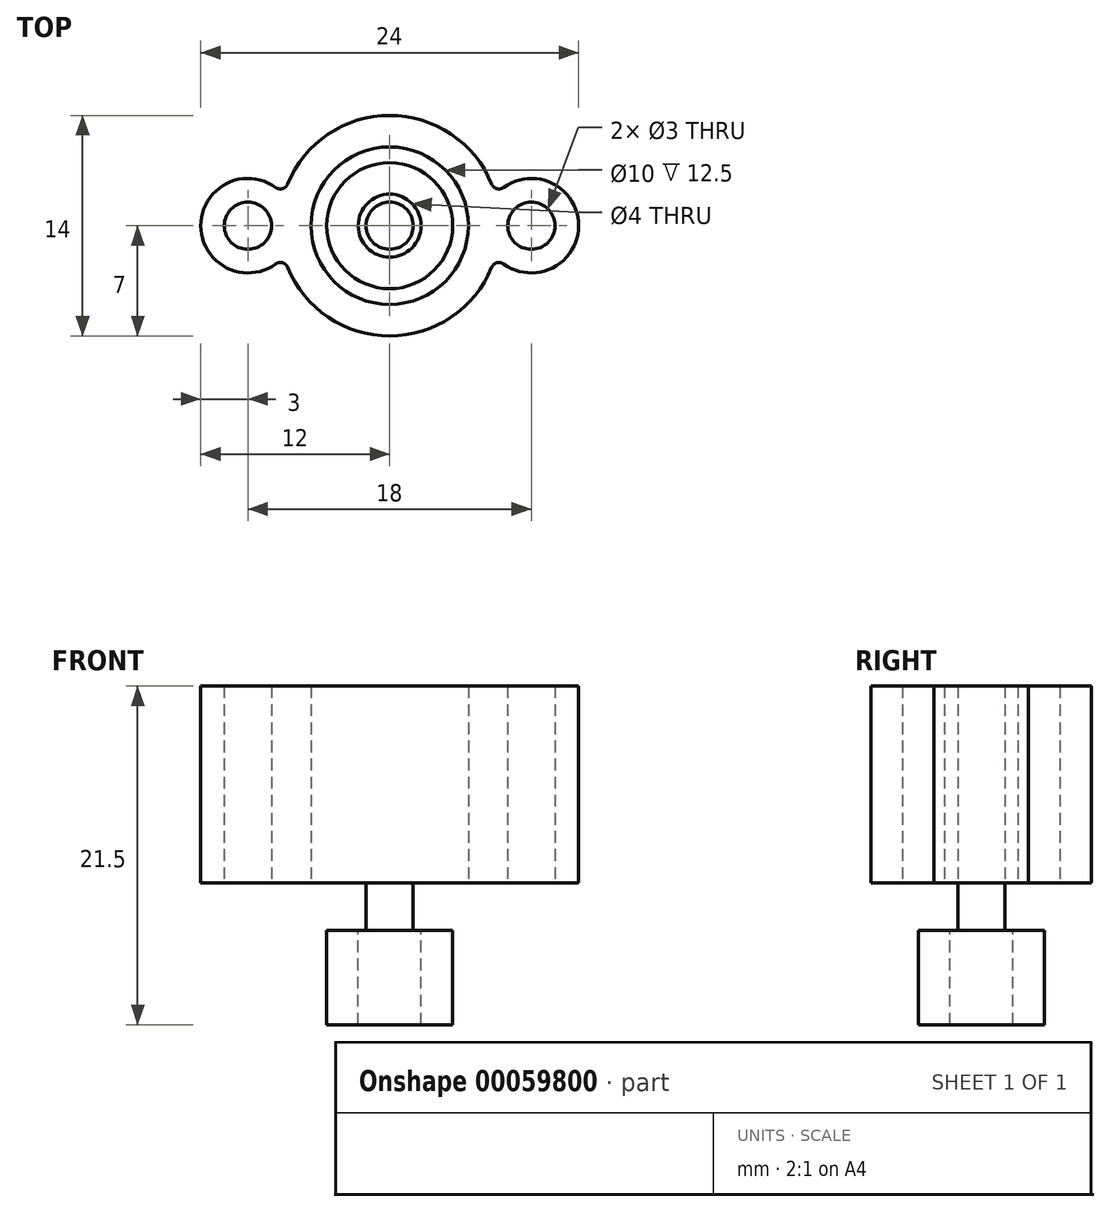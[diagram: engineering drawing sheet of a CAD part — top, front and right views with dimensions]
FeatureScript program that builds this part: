
annotation { "Feature Type Name" : "Feature", "Feature Type Description" : "" }
export const myFeature = defineFeature(function(context is Context, id is Id, definition is map)
    precondition{}
    {
        {
            var Q0;
            Q0=qCreatedBy(makeId("Top.planeOp"),FACE);
            var sketch = newSketch(context, id + "F0", { "sketchPlane" : qUnion([Q0])});
            skCircle(sketch, "E0", {"center": v(9, 0) * mm, "radius": 3 * mm, "construction": true});
            skLineSegment(sketch, "E1", {"start": v(9, 0) * mm, "end": v(0, 0) * mm, "construction": true});
            skLineSegment(sketch, "E2", {"start": v(0, -7) * mm, "end": v(0, 7) * mm, "construction": true});
            skCircle(sketch, "E3", {"center": v(0, 0) * mm, "radius": 7 * mm, "construction": true});
            skArc(sketch, "E4", {"start": v(0, 1.5) * mm, "mid": v(1.5, 0) * mm, "end": v(0, -1.5) * mm});
            skCircle(sketch, "E5", {"center": v(0, 0) * mm, "radius": 1.5 * mm, "construction": true});
            skCircle(sketch, "E6", {"center": v(9, 0) * mm, "radius": 1.5 * mm, "construction": true});
            skLineSegment(sketch, "E7", {"start": v(9, 0) * mm, "end": v(12, 0) * mm, "construction": true});
            skLineSegment(sketch, "E8", {"start": v(15, 0) * mm, "end": v(12, 0) * mm, "construction": true});
            skCircle(sketch, "E9", {"center": v(6.94, 2.83) * mm, "radius": 0.5 * mm, "construction": true});
            skArc(sketch, "E10.trimOffspring", {"start": v(6.48, 2.64) * mm, "mid": v(3.9, 5.8) * mm, "end": v(0, 7) * mm});
            skArc(sketch, "E11", {"start": v(7.24, 2.43) * mm, "mid": v(9.6, 2.94) * mm, "end": v(11.57, 1.55) * mm});
            skArc(sketch, "E12", {"start": v(6.48, 2.64) * mm, "mid": v(6.8, 2.35) * mm, "end": v(7.24, 2.43) * mm});
            skCircle(sketch, "E13", {"center": v(15, 0) * mm, "radius": 3 * mm, "construction": true});
            skCircle(sketch, "E14", {"center": v(15, 0) * mm, "radius": 1.5 * mm, "construction": true});
            skCircle(sketch, "E15", {"center": v(12, 1.8) * mm, "radius": 0.5 * mm, "construction": true});
            skLineSegment(sketch, "E16", {"start": v(12, 1.8) * mm, "end": v(12, 0) * mm, "construction": true});
            skArc(sketch, "E17", {"start": v(11.57, 1.55) * mm, "mid": v(12, 1.3) * mm, "end": v(12.43, 1.55) * mm});
            skLineSegment(sketch, "E18", {"start": v(15, 0) * mm, "end": v(18, 0) * mm, "construction": true});
            skArc(sketch, "E19", {"start": v(12.43, 1.55) * mm, "mid": v(15.8, 2.9) * mm, "end": v(18, 0) * mm});
            skArc(sketch, "E20", {"start": v(13.5, 0) * mm, "mid": v(15, 1.5) * mm, "end": v(16.5, 0) * mm});
            skArc(sketch, "E21.MirrorCS", {"start": v(6.48, -2.64) * mm, "mid": v(3.9, -5.8) * mm, "end": v(0, -7) * mm});
            skArc(sketch, "E22.MirrorCS", {"start": v(6.48, -2.64) * mm, "mid": v(6.8, -2.35) * mm, "end": v(7.24, -2.43) * mm});
            skArc(sketch, "E23.MirrorCS", {"start": v(7.24, -2.43) * mm, "mid": v(9.6, -2.94) * mm, "end": v(11.57, -1.55) * mm});
            skArc(sketch, "E24.MirrorCS", {"start": v(11.57, -1.55) * mm, "mid": v(12, -1.3) * mm, "end": v(12.43, -1.55) * mm});
            skArc(sketch, "E25.MirrorCS", {"start": v(12.43, -1.55) * mm, "mid": v(15.8, -2.9) * mm, "end": v(18, 0) * mm});
            skArc(sketch, "E26.MirrorCS", {"start": v(13.5, 0) * mm, "mid": v(15, -1.5) * mm, "end": v(16.5, 0) * mm});
            skArc(sketch, "E27.MirrorCS", {"start": v(-6.48, 2.64) * mm, "mid": v(-3.9, 5.8) * mm, "end": v(0, 7) * mm});
            skArc(sketch, "E28.MirrorCS", {"start": v(-6.48, -2.64) * mm, "mid": v(-3.9, -5.8) * mm, "end": v(0, -7) * mm});
            skArc(sketch, "E29.MirrorCS", {"start": v(-6.48, -2.64) * mm, "mid": v(-6.8, -2.35) * mm, "end": v(-7.24, -2.43) * mm});
            skArc(sketch, "E30.MirrorCS", {"start": v(-6.48, 2.64) * mm, "mid": v(-6.8, 2.35) * mm, "end": v(-7.24, 2.43) * mm});
            skArc(sketch, "E31.MirrorCS", {"start": v(-7.24, 2.43) * mm, "mid": v(-9.6, 2.94) * mm, "end": v(-11.57, 1.55) * mm});
            skArc(sketch, "E32.MirrorCS", {"start": v(-11.57, 1.55) * mm, "mid": v(-12, 1.3) * mm, "end": v(-12.43, 1.55) * mm});
            skArc(sketch, "E33.MirrorCS", {"start": v(-11.57, -1.55) * mm, "mid": v(-12, -1.3) * mm, "end": v(-12.43, -1.55) * mm});
            skArc(sketch, "E34.MirrorCS", {"start": v(-7.24, -2.43) * mm, "mid": v(-9.6, -2.94) * mm, "end": v(-11.57, -1.55) * mm});
            skArc(sketch, "E35.MirrorCS", {"start": v(-12.43, -1.55) * mm, "mid": v(-15.8, -2.9) * mm, "end": v(-18, 0) * mm});
            skArc(sketch, "E36.MirrorCS", {"start": v(-12.43, 1.55) * mm, "mid": v(-15.8, 2.9) * mm, "end": v(-18, 0) * mm});
            skArc(sketch, "E37.MirrorCS", {"start": v(-13.5, 0) * mm, "mid": v(-15, 1.5) * mm, "end": v(-16.5, 0) * mm});
            skArc(sketch, "E38.MirrorCS", {"start": v(-13.5, 0) * mm, "mid": v(-15, -1.5) * mm, "end": v(-16.5, 0) * mm});
            skCircle(sketch, "E39.MirrorC", {"center": v(-9, 0) * mm, "radius": 1.5 * mm, "construction": true});
            skArc(sketch, "E40.MirrorCS", {"start": v(0, 1.5) * mm, "mid": v(-1.5, 0) * mm, "end": v(0, -1.5) * mm});
            skSolve(sketch);
        }
        {
            var Q0;
            Q0=makeQuery(id+"F0.imprint","IMPRINT",FACE,{"disambiguationData":[TD([[makeQuery(id+"F0.imprint","IMPRINT",EDGE,{"derivedFrom":sQuery(id+"F0.wireOp",EDGE,"E4")}),1.0]])]});
            extrude(context, id + "F1", {"entities" : qUnion([Q0]), "depth" : 3 * mm});
        }
        {
            var Q0;
            Q0=makeQuery(id+"F1.opExtrude","CAP_FACE",FACE,{"disambiguationData":[OSD([sQuery(id+"F0.wireOp",EDGE,"E4"),sQuery(id+"F0.wireOp",EDGE,"E10.trimOffspring"),sQuery(id+"F0.wireOp",EDGE,"E11"),sQuery(id+"F0.wireOp",EDGE,"E12"),sQuery(id+"F0.wireOp",EDGE,"E17"),sQuery(id+"F0.wireOp",EDGE,"E19"),sQuery(id+"F0.wireOp",EDGE,"E20"),sQuery(id+"F0.wireOp",EDGE,"E21.MirrorCS"),sQuery(id+"F0.wireOp",EDGE,"E22.MirrorCS"),sQuery(id+"F0.wireOp",EDGE,"E23.MirrorCS"),sQuery(id+"F0.wireOp",EDGE,"E24.MirrorCS"),sQuery(id+"F0.wireOp",EDGE,"E25.MirrorCS"),sQuery(id+"F0.wireOp",EDGE,"E26.MirrorCS"),sQuery(id+"F0.wireOp",EDGE,"E27.MirrorCS"),sQuery(id+"F0.wireOp",EDGE,"E28.MirrorCS"),sQuery(id+"F0.wireOp",EDGE,"E29.MirrorCS"),sQuery(id+"F0.wireOp",EDGE,"E30.MirrorCS"),sQuery(id+"F0.wireOp",EDGE,"E31.MirrorCS"),sQuery(id+"F0.wireOp",EDGE,"E32.MirrorCS"),sQuery(id+"F0.wireOp",EDGE,"E33.MirrorCS"),sQuery(id+"F0.wireOp",EDGE,"E34.MirrorCS"),sQuery(id+"F0.wireOp",EDGE,"E35.MirrorCS"),sQuery(id+"F0.wireOp",EDGE,"E36.MirrorCS"),sQuery(id+"F0.wireOp",EDGE,"E37.MirrorCS"),sQuery(id+"F0.wireOp",EDGE,"E38.MirrorCS"),sQuery(id+"F0.wireOp",EDGE,"E40.MirrorCS")])],"isStart":false});
            var sketch = newSketch(context, id + "F2", { "sketchPlane" : qUnion([Q0])});
            skArc(sketch, "E41", {"start": v(6.48, 2.64) * mm, "mid": v(3.9, 5.8) * mm, "end": v(0, 7) * mm});
            skArc(sketch, "E42", {"start": v(7.24, -2.43) * mm, "mid": v(12, 0) * mm, "end": v(7.24, 2.43) * mm});
            skArc(sketch, "E43", {"start": v(6.48, 2.64) * mm, "mid": v(6.8, 2.35) * mm, "end": v(7.24, 2.43) * mm});
            skArc(sketch, "E44", {"start": v(6.48, -2.64) * mm, "mid": v(6.8, -2.35) * mm, "end": v(7.24, -2.43) * mm});
            skLineSegment(sketch, "E45", {"start": v(0, 7) * mm, "end": v(0, -7) * mm, "construction": true});
            skArc(sketch, "E46.trimOffspring", {"start": v(0, -7) * mm, "mid": v(3.9, -5.8) * mm, "end": v(6.48, -2.64) * mm});
            skArc(sketch, "E47", {"start": v(0, 5) * mm, "mid": v(5, 0) * mm, "end": v(0, -5) * mm});
            skCircle(sketch, "E48.0", {"center": v(9, 0) * mm, "radius": 1.5 * mm});
            skLineSegment(sketch, "E49", {"start": v(0, 0) * mm, "end": v(12, 0) * mm, "construction": true});
            skArc(sketch, "E50.MirrorCS", {"start": v(0, 5) * mm, "mid": v(-5, 0) * mm, "end": v(0, -5) * mm});
            skArc(sketch, "E51.MirrorCS", {"start": v(-6.48, 2.64) * mm, "mid": v(-3.9, 5.8) * mm, "end": v(0, 7) * mm});
            skArc(sketch, "E52.MirrorCS", {"start": v(-6.48, 2.64) * mm, "mid": v(-6.8, 2.35) * mm, "end": v(-7.24, 2.43) * mm});
            skArc(sketch, "E53.MirrorCS", {"start": v(-7.24, -2.43) * mm, "mid": v(-12, 0) * mm, "end": v(-7.24, 2.43) * mm});
            skArc(sketch, "E54.MirrorCS", {"start": v(-6.48, -2.64) * mm, "mid": v(-6.8, -2.35) * mm, "end": v(-7.24, -2.43) * mm});
            skArc(sketch, "E55.MirrorCS", {"start": v(0, -7) * mm, "mid": v(-3.9, -5.8) * mm, "end": v(-6.48, -2.64) * mm});
            skCircle(sketch, "E56.MirrorC", {"center": v(-9, 0) * mm, "radius": 1.5 * mm});
            skSolve(sketch);
        }
        {
            var Q0;
            Q0 = qSketchRegion(id + "F2", true);
            extrude(context, id + "F3", {"entities" : qUnion([Q0]), "operationType" : NewBodyOperationType.ADD, "depth" : 12.5 * mm});
        }
        {
            var Q0;
            Q0=makeQuery(id+"F0.imprint","IMPRINT",FACE,{"disambiguationData":[TD([[makeQuery(id+"F0.imprint","IMPRINT",EDGE,{"derivedFrom":sQuery(id+"F0.wireOp",EDGE,"E4")}),1.0]])]});
            var sketch = newSketch(context, id + "F4", { "sketchPlane" : qUnion([Q0])});
            skCircle(sketch, "E57", {"center": v(0, 0) * mm, "radius": 2 * mm});
            skCircle(sketch, "E58", {"center": v(0, 0) * mm, "radius": 4 * mm});
            skSolve(sketch);
        }
        {
            var Q0;
            Q0 = qSketchRegion(id + "F4", true);
            extrude(context, id + "F5", {"entities" : qUnion([Q0]), "operationType" : NewBodyOperationType.ADD, "oppositeDirection" : true, "depth" : 6 * mm});
        }
    });
